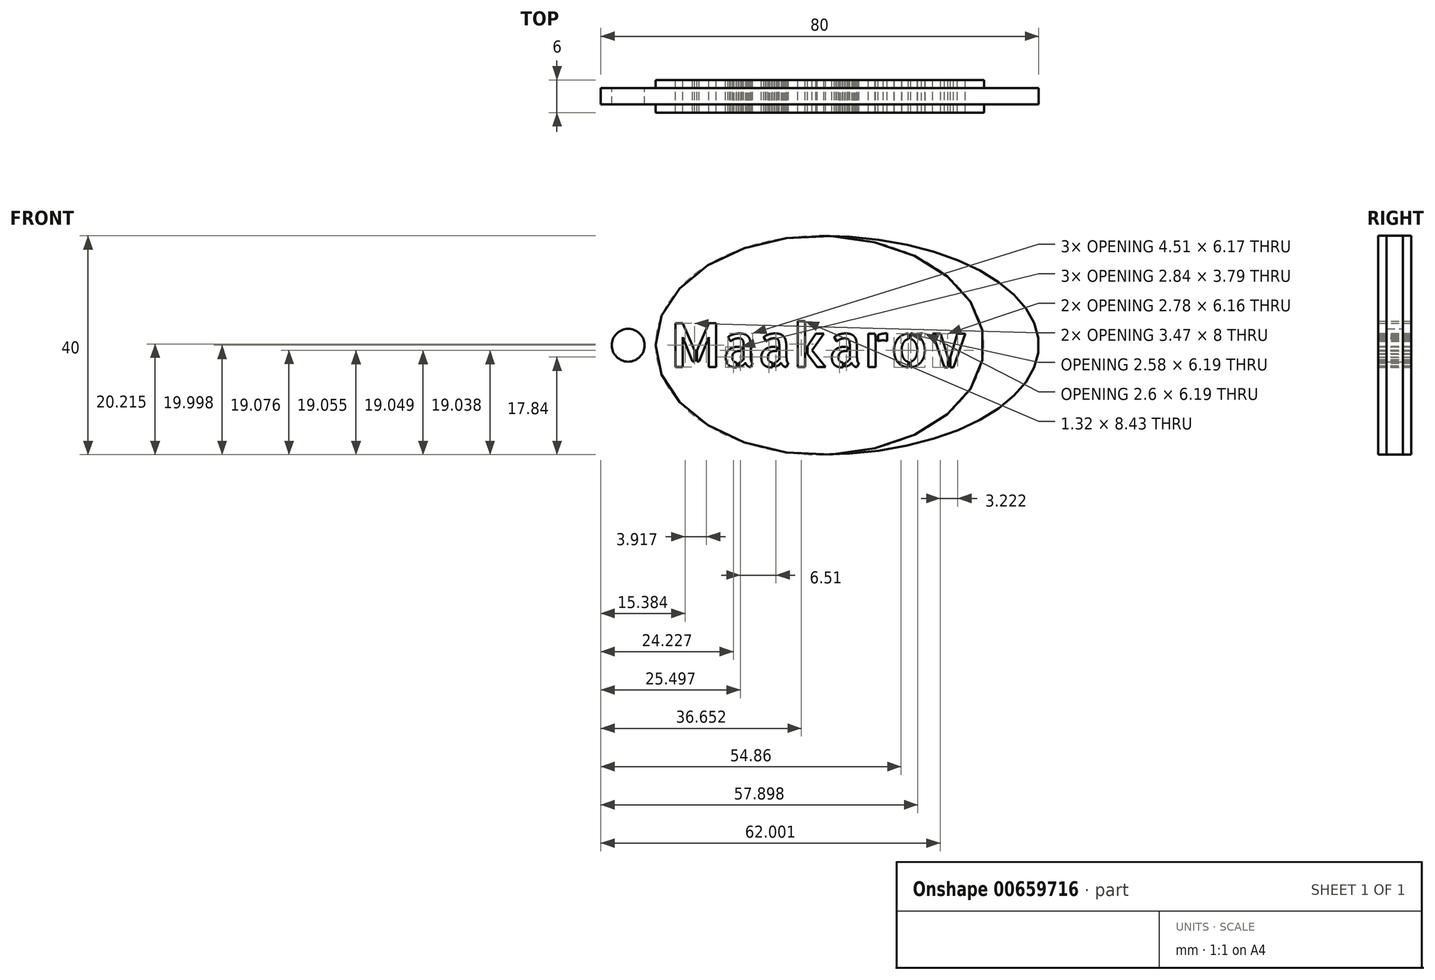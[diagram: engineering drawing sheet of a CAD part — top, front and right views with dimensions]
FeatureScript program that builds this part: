
annotation { "Feature Type Name" : "Feature", "Feature Type Description" : "" }
export const myFeature = defineFeature(function(context is Context, id is Id, definition is map)
    precondition{}
    {
        {
            var Q0;
            Q0=qCreatedBy(makeId("Front.planeOp"),FACE);
            var sketch = newSketch(context, id + "F0", { "sketchPlane" : qUnion([Q0])});
            skPoint(sketch, "E0.middle", {"position": v(0, 0) * mm});
            skEllipse(sketch, "E1", {"center": v(0, 0) * mm, "majorRadius": 30 * mm, "minorRadius": 20 * mm, "majorAxis": v(-1, 0)});
            skText(sketch, "E2", { "text": "Maakarov", "fontName": "AllertaStencil-Regular.ttf"});
            skEllipse(sketch, "E3", {"center": v(0, 0) * mm, "majorRadius": 40 * mm, "minorRadius": 20 * mm, "majorAxis": v(-1, 0)});
            skCircle(sketch, "E4", {"center": v(-35, 0) * mm, "radius": 3 * mm});
            skPoint(sketch, "E4.centerSnap0", {"position": v(-40, 0) * mm});
            skPoint(sketch, "E5", {"position": v(-30, 0) * mm});
            const initialGuessF0  = {"E2": [-0.02735, -0.004, 1, 0, 0.008]};
            skSetInitialGuess(sketch, initialGuessF0);
            skSolve(sketch);
        }
        {
            var Q0;
            Q0=makeQuery(id+"F0.imprint","IMPRINT",FACE,{"disambiguationData":[TD([[makeQuery(id+"F0.imprint","IMPRINT",EDGE,{"derivedFrom":sQuery(id+"F0.wireOp",EDGE,"E2.sketch_text.stroke-0")}),1.0]])]});
            var Q1;
            Q1=sQuery(id+"F0.wireOp",EDGE,"E1");
            extrude(context, id + "F1", {"entities" : qUnion([Q0]), "surfaceEntities" : qUnion([Q1]), "endBound" : BoundingType.SYMMETRIC, "depth" : 6 * mm, "offsetDistance" : 25 * mm});
        }
        {
            var Q0;
            Q0=makeQuery(id+"F0.imprint","IMPRINT",FACE,{"disambiguationData":[TD([[makeQuery(id+"F0.imprint","IMPRINT",EDGE,{"derivedFrom":sQuery(id+"F0.wireOp",EDGE,"E4")}),-1.0]])]});
            var Q1;
            {var subQ0=sQuery(id+"F0.wireOp",EDGE,"E3");var subQ1=sQuery(id+"F0.wireOp",EDGE,"E1");var subQ2=makeQuery(id+"F0.imprint","INTERSECT",VERTEX,{"disambiguationData":[OD(0.0)],"derivedFrom":[subQ1,subQ0]});Q1=makeQuery(id+"F0.imprint","IMPRINT",FACE,{"disambiguationData":[TD([[makeQuery(id+"F0.imprint","IMPRINT",EDGE,{"disambiguationData":[TD([[subQ2,-1.0]])],"derivedFrom":subQ1}),-1.0]])]});}
            extrude(context, id + "F2", {"entities" : qUnion([Q0, Q1]), "operationType" : NewBodyOperationType.ADD, "endBound" : BoundingType.SYMMETRIC, "depth" : 3 * mm, "offsetDistance" : 25 * mm});
        }
    });
